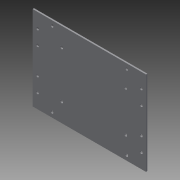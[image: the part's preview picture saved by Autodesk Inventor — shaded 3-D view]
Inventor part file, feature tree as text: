
AUTODESK INVENTOR PART (.ipt)
format: ipt  version: 2014 (Build 180170000, 170)  size: 138,240 bytes
history: native  units: mm
features: sketch x4, hole x3, other x1, extrude x1
ambient origin geometry x8: Origin, YZ Plane, XZ Plane, XY Plane, X Axis, Y Axis, Z Axis, Center Point
bodies: Body1 (feature_tree)
feature tree (9):
  other  "ソリッド1"
  extrude  "押し出し1"  Depth=117.0mm
  hole  "穴1"  [1 undecoded]
  hole  "穴2"  [1 undecoded]
  hole  "穴3"  [1 undecoded]
  sketch  "スケッチ1"
  sketch  "スケッチ2"
  sketch  "スケッチ3"
  sketch  "スケッチ4"
note: 3 required parameter values undecoded (feature->parameter linkage not recoverable at this tier; creation-order binding heuristic only, values carry confidence <= 0.55)
